# Revit family: RJ45ADAPTER
name_source: partatom
category: Data Devices
units: mm (PartAtom-declared; Revit-internal decimal feet)

## family parameters
Cut with Voids When Loaded = No
Host = Face
Maintain Annotation Orientation = No
OmniClass Number = 23.85.50.17.11
OmniClass Title = Computer Network Equipment
Part Type = Normal
Room Calculation Point = No
Round Connector Dimension = Use Diameter
Shared = No

## types (1)
- RJ45 Adapter
    Angle = 75.00°
    Apparent Load = 0 VA
    Assembly Code = D5030600
    Certifications = cULus listed
    Connector Description 1 = Power Supply
    Connector Description 2 = Data
    Construction = SABIC NORYL HS2000X
    Default Elevation = 48 "
    Description = RJ45 Adapter and CAT5 System Cables
    Door is Open = Yes
    Electrical = 4 Terminal Connectors-Red: +24V; Blue: Occupancy Sensor Input; Yellow: Photocell/Daylight Sensor Input; Black: Common
    Load Classification = Power
    Manufacturer = NX Lighting Controls
    Model = RJ45ADAPTER
    Mounting = Adapter may be mounted using a zip-tie (not included) or with a #8 or #10 mounting screw (not included).
    Number of Poles = 1
    Plenum Rated = RJ45ADAPTER and Cables are UL2043 compliant (Plenum rated)
    Power Factor = 1
    Product Material = Gray
    Type Comments = Data Devices
    URL = https://www.currentlighting.com
    Voltage = 120 V
    Warranty = Five-year limited
    Weight = 0.00 kg

## geometry (parser evidence)
native form markers: Sweep x2
no freeform markers — native parametric forms only
